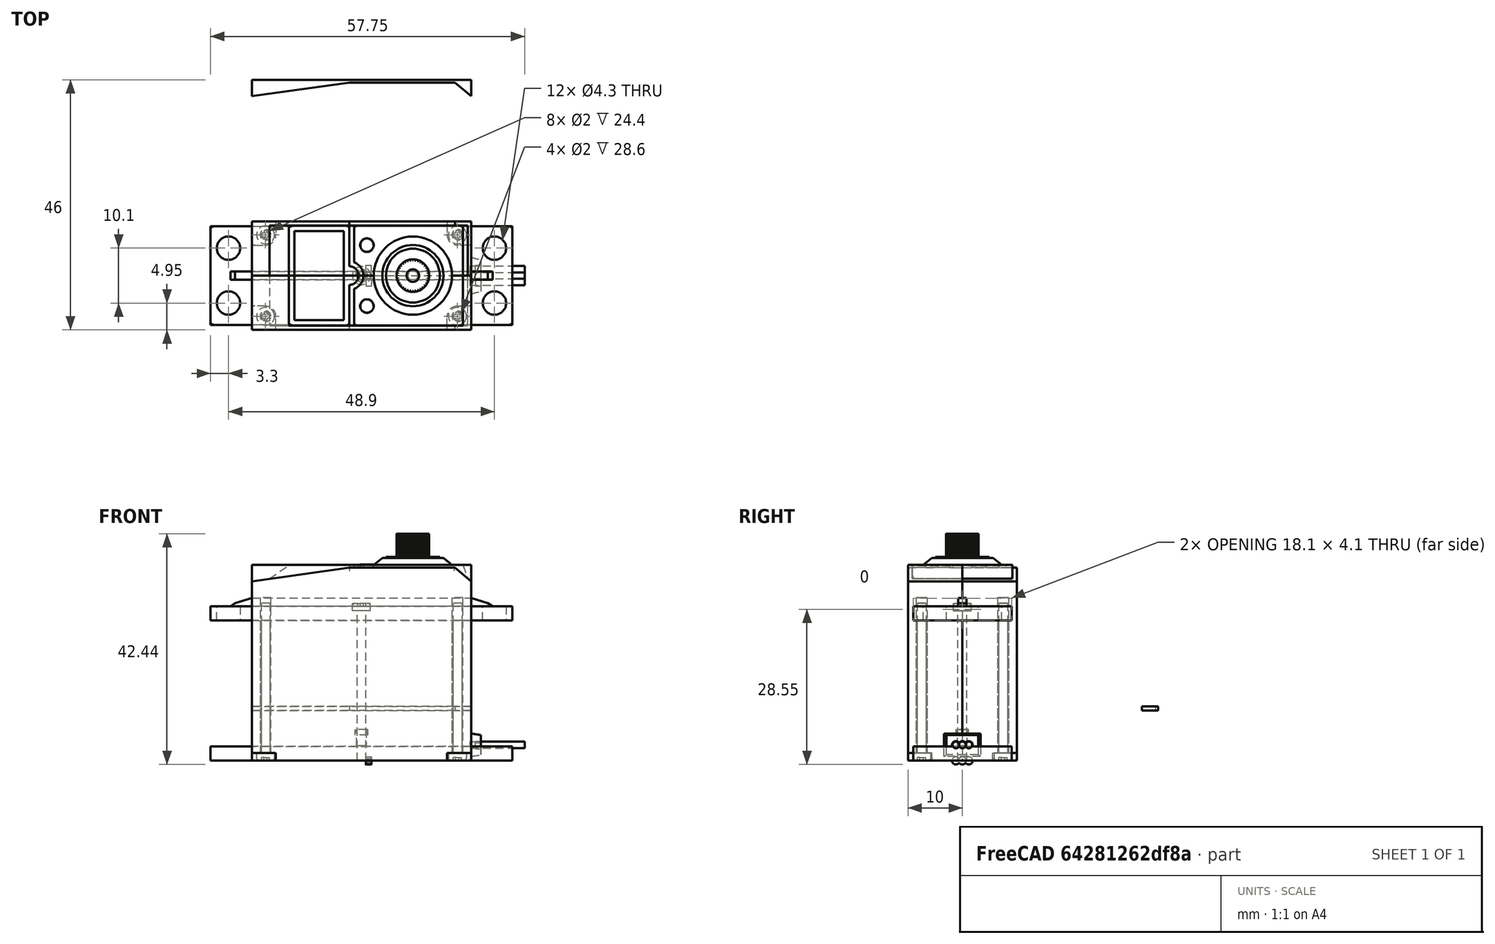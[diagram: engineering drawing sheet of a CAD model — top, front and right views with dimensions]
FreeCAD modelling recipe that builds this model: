
FCSTD DOCUMENT  (FreeCAD 0.15R4671 (Git))
Label: Futaba3003
Comment: It has been modeled using a caliper and a real Futaba 3003 servo
License: CC-BY 3.0
LicenseURL: http://creativecommons.org/licenses/by/3.0/
objects: Sketcher::SketchObject×24, PartDesign::Pocket×12, Part::Feature×12, Part::MultiFuse×7, App::DocumentObjectGroup×6, PartDesign::Pad×5, Part::Loft×3, Part::Cylinder×3, Part::Mirroring×2, Part::Fillet×2, PartDesign::PolarPattern×1, PartDesign::Revolution×1, PartDesign::Fillet×1, PartDesign::Mirrored×1, Part::Cut×1, Part::Compound×1
note: 94 computed .brp shape members not serialized (recipe doc carries the construction recipe); baked Part::Feature solids carry a one-line shape summary decoded from their .brp

FEATURE [Sketcher::SketchObject] Sketch  label="body-sketch"
  Placement = pos=(0,0,0) rot=(1,0,0;1.5708rad)
  sketch-geometry (4):
    g0: LineSegment StartX=-20.15 StartY=36 StartZ=0 EndX=20.15 EndY=36 EndZ=0
    g1: LineSegment StartX=20.15 StartY=0 StartZ=0 EndX=-20.15 EndY=0 EndZ=0
    g2: LineSegment StartX=-20.15 StartY=0 StartZ=0 EndX=-20.15 EndY=36 EndZ=0
    g3: LineSegment StartX=20.15 StartY=36 StartZ=0 EndX=20.15 EndY=0 EndZ=0
  constraints (11):
    c: Coincident(g3,g1)
    c: Coincident(g1,g2)
    c: Horizontal(g0)
    c: Horizontal(g1)
    c: Vertical(g2)
    c: Symmetric(g0,g0,g-2)
    c: PointOnObject(g3,g-1)
    c: DistanceX(g0) = 40.3
    c: DistanceY(g0,g1) = -36
    c: Coincident(g2,g0)
    c: Coincident(g3,g0)
FEATURE [PartDesign::Pad] Pad  label="main_body"
  Length = 10
  Length2 = 100
  Placement = pos=(0,0,0) rot=(1,0,0;1.5708rad)
  Sketch = -> Sketch
  Type = 0
FEATURE [Sketcher::SketchObject] Sketch001  label="lateral-layer1-sketch"
  ExternalGeometry = -> [Pad]
  Placement = pos=(0,-10,0) rot=(1,0,0;1.5708rad)
  Support = -> Pad [Face14]
  sketch-geometry (6):
    g0: LineSegment StartX=20.15 StartY=33 StartZ=0 EndX=17.18 EndY=35.52 EndZ=0
    g1: LineSegment StartX=17.18 StartY=35.52 StartZ=0 EndX=-2.25 EndY=35.52 EndZ=0
    g2: LineSegment StartX=-2.25 StartY=35.52 StartZ=0 EndX=-20.15 EndY=33 EndZ=0
    g3: LineSegment StartX=-20.15 StartY=33 StartZ=0 EndX=-20.15 EndY=36 EndZ=0
    g4: LineSegment StartX=-20.15 StartY=36 StartZ=0 EndX=20.15 EndY=36 EndZ=0
    g5: LineSegment StartX=20.15 StartY=36 StartZ=0 EndX=20.15 EndY=33 EndZ=0
  constraints (16):
    c: Coincident(g0,g1)
    c: Horizontal(g1)
    c: Coincident(g1,g2)
    c: Coincident(g3,g2)
    c: Coincident(g4,g3)
    c: DistanceY(g0) = 33
    c: DistanceY(g4,g0) = -0.48
    c: DistanceX(g0,g0) = -2.97
    c: DistanceX(g4,g1) = -22.4
    c: Coincident(g5,g4)
    c: Coincident(g5,g0)
    c: PointOnObject(g0,g-4)
    c: Coincident(g4,g-4)
    c: Coincident(g3,g-3)
    c: PointOnObject(g2,g-3)
    c: DistanceY(g-1,g2) = 33
FEATURE [Sketcher::SketchObject] Sketch003
  Placement = pos=(0,0,0) rot=(0.57735,0.57735,0.57735;2.0944rad)
  sketch-geometry (4):
    g0: LineSegment StartX=-3.35 StartY=2.1 StartZ=0 EndX=3.35 EndY=2.1 EndZ=0
    g1: LineSegment StartX=3.35 StartY=2.1 StartZ=0 EndX=3.35 EndY=-2.1 EndZ=0
    g2: LineSegment StartX=3.35 StartY=-2.1 StartZ=0 EndX=-3.35 EndY=-2.1 EndZ=0
    g3: LineSegment StartX=-3.35 StartY=-2.1 StartZ=0 EndX=-3.35 EndY=2.1 EndZ=0
  constraints (12):
    c: Coincident(g0,g1)
    c: Coincident(g2,g3)
    c: Coincident(g3,g0)
    c: Horizontal(g0)
    c: Horizontal(g2)
    c: Vertical(g1)
    c: Vertical(g3)
    c: Symmetric(g0,g0,g-2)
    c: Coincident(g1,g2)
    c: DistanceY(g1) = -4.2
    c: DistanceX(g0) = 6.7
    c: Symmetric(g0,g2,g-1)
FEATURE [Sketcher::SketchObject] Sketch004
  Placement = pos=(1.8,0,0) rot=(0.57735,0.57735,0.57735;2.0944rad)
  sketch-geometry (4):
    g0: LineSegment StartX=-2.9 StartY=1.825 StartZ=0 EndX=2.9 EndY=1.825 EndZ=0
    g1: LineSegment StartX=2.9 StartY=1.825 StartZ=0 EndX=2.9 EndY=-1.825 EndZ=0
    g2: LineSegment StartX=2.9 StartY=-1.825 StartZ=0 EndX=-2.9 EndY=-1.825 EndZ=0
    g3: LineSegment StartX=-2.9 StartY=-1.825 StartZ=0 EndX=-2.9 EndY=1.825 EndZ=0
  constraints (12):
    c: Coincident(g0,g1)
    c: Coincident(g2,g3)
    c: Coincident(g3,g0)
    c: Horizontal(g0)
    c: Horizontal(g2)
    c: Vertical(g1)
    c: Vertical(g3)
    c: Symmetric(g0,g0,g-2)
    c: Coincident(g1,g2)
    c: DistanceY(g1) = -3.65
    c: DistanceX(g0) = 5.8
    c: Symmetric(g0,g2,g-1)
FEATURE [Part::Loft] Loft  label="wire-holder-body"
  Closed = false
  Placement = pos=(20.15,0,2.9) rot=(0,0,1;0rad)
  Ruled = false
  Sections = -> [Sketch003,Sketch004]
  Solid = true
FEATURE [Part::Cylinder] Cylinder  label="red-wire"
  Angle = 360
  Height = 10
  Placement = pos=(0,0,0) rot=(0,1,0;1.5708rad)
  Radius = 0.6
FEATURE [Part::Cylinder] Cylinder001  label="white-wire"
  Angle = 360
  Height = 10
  Placement = pos=(0,1.2,0) rot=(0,1,0;1.5708rad)
  Radius = 0.6
FEATURE [Part::Cylinder] Cylinder002  label="blck-wire"
  Angle = 360
  Height = 10
  Placement = pos=(0,-1.2,0) rot=(0,1,0;1.5708rad)
  Radius = 0.6
FEATURE [Sketcher::SketchObject] Sketch005
  ExternalGeometry = -> [Loft]
  Placement = pos=(21.95,0,2.9) rot=(0.57735,0.57735,0.57735;2.0944rad)
  Support = -> Loft [Face6]
  sketch-geometry (6):
    g0: LineSegment [constr] StartX=-1.2 StartY=0 StartZ=0 EndX=1.2 EndY=0 EndZ=0
    g1: ArcOfCircle CenterX=-1.2 CenterY=0 CenterZ=0 NormalX=0 NormalY=0 NormalZ=1 Radius=0.7 StartAngle=0.5411 EndAngle=5.74209
    g2: ArcOfCircle CenterX=0 CenterY=0 CenterZ=0 NormalX=0 NormalY=0 NormalZ=1 Radius=0.7 StartAngle=0.5411 EndAngle=2.60049
    g3: ArcOfCircle CenterX=0 CenterY=0 CenterZ=0 NormalX=0 NormalY=0 NormalZ=1 Radius=0.7 StartAngle=3.68269 EndAngle=5.74209
    g4: ArcOfCircle CenterX=1.2 CenterY=0 CenterZ=0 NormalX=0 NormalY=0 NormalZ=1 Radius=0.7 StartAngle=3.68269 EndAngle=8.88368
    g5: LineSegment [constr] StartX=-1.2 StartY=0 StartZ=0 EndX=-1.2 EndY=-0.7 EndZ=0
  constraints (20):
    c: Horizontal(g0)
    c: Symmetric(g0,g0,g-2)
    c: Coincident(g1,g0)
    c: PointOnObject(g2,g0)
    c: Coincident(g2,g1)
    c: PointOnObject(g2,g-2)
    c: Coincident(g3,g2)
    c: Coincident(g3,g1)
    c: Coincident(g4,g0)
    c: Coincident(g4,g2)
    c: Coincident(g4,g3)
    c: Equal(g1,g2)
    c: Equal(g2,g4)
    c: Equal(g4,g3)
    c: DistanceX(g2,g0) = 1.2
    c: Coincident(g5,g0)
    c: Vertical(g5)
    c: PointOnObject(g5,g1)
    c: Radius(g4) = 0.7
    c: PointOnObject(g0,g-1)
FEATURE [PartDesign::Pocket] Pocket002  label="wire-holder"
  Length = 1
  Placement = pos=(20.15,0,2.9) rot=(0,0,1;0rad)
  Sketch = -> Sketch005
  Type = 0
FEATURE [App::DocumentObjectGroup] Group  label="servo-wire-holder"
  Group = -> [Pocket002,Loft]
FEATURE [PartDesign::Pocket] Pocket  label="lateral-layer1"
  Length = 0.8
  Placement = pos=(0,0,0) rot=(1,0,0;1.5708rad)
  Sketch = -> Sketch001
  Type = 0
FEATURE [Sketcher::SketchObject] Sketch002  label="lateral-layer2-sketch"
  Placement = pos=(0,-9.2,0) rot=(1,0,0;1.5708rad)
  Support = -> Pocket [Face4]
  sketch-geometry (12):
    g0: GeomPoint [constr] X=19.55 Y=33.5091 Z=0
    g1: GeomPoint [constr] X=18.65 Y=36 Z=0
    g2: LineSegment StartX=18.65 StartY=36 StartZ=0 EndX=19.55 EndY=33.5091 EndZ=0
    g3: LineSegment StartX=19.55 StartY=33.5091 StartZ=0 EndX=20.15 EndY=33 EndZ=0
    g4: LineSegment StartX=18.65 StartY=36 StartZ=0 EndX=20.15 EndY=36 EndZ=0
    g5: LineSegment StartX=20.15 StartY=36 StartZ=0 EndX=20.15 EndY=33 EndZ=0
    g6: GeomPoint [constr] X=-16.9 Y=33.4575 Z=0
    g7: GeomPoint [constr] X=-13.35 Y=36 Z=0
    g8: LineSegment StartX=-20.15 StartY=33 StartZ=0 EndX=-16.9 EndY=33.4575 EndZ=0
    g9: LineSegment StartX=-16.9 StartY=33.4575 StartZ=0 EndX=-13.35 EndY=36 EndZ=0
    g10: LineSegment StartX=-20.15 StartY=33 StartZ=0 EndX=-20.15 EndY=36 EndZ=0
    g11: LineSegment StartX=-20.15 StartY=36 StartZ=0 EndX=-13.35 EndY=36 EndZ=0
  constraints (16):
    c: Coincident(g2,g1)
    c: Coincident(g2,g0)
    c: Coincident(g4,g1)
    c: Coincident(g5,g4)
    c: Coincident(g5,g3)
    c: Coincident(g3,g0)
    c: Coincident(g8,g6)
    c: Coincident(g9,g6)
    c: Coincident(g9,g7)
    c: DistanceX(g8,g6) = 3.25
    c: DistanceX(g7,g4) = 33.5
    c: Coincident(g10,g8)
    c: Coincident(g11,g10)
    c: Coincident(g11,g7)
    c: DistanceX(g4,g0) = -0.6
    c: DistanceX(g1,g4) = 1.5
FEATURE [PartDesign::Pocket] Pocket003  label="lateral-layer2"
  Length = 5
  Placement = pos=(0,0,0) rot=(1,0,0;1.5708rad)
  Sketch = -> Sketch002
  Type = 1
FEATURE [Part::Mirroring] Part__Mirroring  label="lateral-layer2 (Mirror #1)"
  Base = (0,0,0)
  Normal = (0,1,0)
  Source = -> Pocket003
FEATURE [Sketcher::SketchObject] Sketch006  label="ear-body-sketch"
  sketch-geometry (4):
    g0: LineSegment StartX=-27.75 StartY=9.05 StartZ=0 EndX=27.75 EndY=9.05 EndZ=0
    g1: LineSegment StartX=27.75 StartY=9.05 StartZ=0 EndX=27.75 EndY=-9.05 EndZ=0
    g2: LineSegment StartX=27.75 StartY=-9.05 StartZ=0 EndX=-27.75 EndY=-9.05 EndZ=0
    g3: LineSegment StartX=-27.75 StartY=-9.05 StartZ=0 EndX=-27.75 EndY=9.05 EndZ=0
  constraints (11):
    c: Coincident(g0,g1)
    c: Coincident(g1,g2)
    c: Coincident(g2,g3)
    c: Coincident(g3,g0)
    c: Horizontal(g0)
    c: Horizontal(g2)
    c: Vertical(g1)
    c: Vertical(g3)
    c: Symmetric(g0,g1,g-1)
    c: DistanceX(g0) = 55.5
    c: DistanceY(g1) = -18.1
FEATURE [PartDesign::Pad] Pad001  label="ear-body"
  Length = 2.6
  Length2 = 100
  Sketch = -> Sketch006
  Type = 0
FEATURE [Sketcher::SketchObject] Sketch007  label="ear-holes-sketch"
  Placement = pos=(0,0,2.6) rot=(0,0,1;0rad)
  Support = -> Pad001 [Face6]
  sketch-geometry (12):
    g0: Circle CenterX=-24.45 CenterY=5.05 CenterZ=0 NormalX=0 NormalY=0 NormalZ=1 Radius=2.15
    g1: Circle CenterX=-24.45 CenterY=-5.05 CenterZ=0 NormalX=0 NormalY=0 NormalZ=1 Radius=2.15
    g2: Circle CenterX=24.45 CenterY=5.05 CenterZ=0 NormalX=0 NormalY=0 NormalZ=1 Radius=2.15
    g3: Circle CenterX=24.45 CenterY=-5.05 CenterZ=0 NormalX=0 NormalY=0 NormalZ=1 Radius=2.15
    g4: LineSegment [constr] StartX=-24.45 StartY=5.05 StartZ=0 EndX=24.45 EndY=5.05 EndZ=0
    g5: LineSegment [constr] StartX=24.45 StartY=5.05 StartZ=0 EndX=24.45 EndY=-5.05 EndZ=0
    g6: LineSegment [constr] StartX=24.45 StartY=-5.05 StartZ=0 EndX=-24.45 EndY=-5.05 EndZ=0
    g7: LineSegment [constr] StartX=-24.45 StartY=-5.05 StartZ=0 EndX=-24.45 EndY=5.05 EndZ=0
    g8: GeomPoint [constr] X=-24.45 Y=2.9 Z=0
    g9: GeomPoint [constr] X=-22.3 Y=5.05 Z=0
    g10: GeomPoint [constr] X=-24.45 Y=-2.9 Z=0
    g11: GeomPoint [constr] X=22.3 Y=5.05 Z=0
  constraints (27):
    c: Coincident(g4,g5)
    c: Coincident(g5,g6)
    c: Coincident(g6,g7)
    c: Coincident(g7,g4)
    c: Horizontal(g4)
    c: Horizontal(g6)
    c: Vertical(g5)
    c: Vertical(g7)
    c: Symmetric(g4,g5,g-1)
    c: Coincident(g2,g4)
    c: Coincident(g3,g5)
    c: Coincident(g1,g6)
    c: Coincident(g0,g4)
    c: PointOnObject(g8,g7)
    c: PointOnObject(g9,g4)
    c: PointOnObject(g8,g0)
    c: PointOnObject(g9,g0)
    c: Equal(g0,g1)
    c: Equal(g1,g2)
    c: Equal(g2,g3)
    c: Radius(g0) = 2.15
    c: PointOnObject(g10,g7)
    c: PointOnObject(g10,g1)
    c: DistanceY(g8,g10) = -5.8
    c: PointOnObject(g11,g4)
    c: PointOnObject(g11,g2)
    c: DistanceX(g9,g11) = 44.6
FEATURE [PartDesign::Pocket] Pocket004  label="ear-holes"
  Length = 5
  Sketch = -> Sketch007
  Type = 1
FEATURE [Sketcher::SketchObject] Sketch008  label="nose-sketch"
  Placement = pos=(0,0,2.6) rot=(1,0,0;1.5708rad)
  sketch-geometry (6):
    g0: LineSegment StartX=-24.1 StartY=0 StartZ=0 EndX=-23.23 EndY=0.6 EndZ=0
    g1: LineSegment StartX=-23.23 StartY=0.6 StartZ=0 EndX=-20.15 EndY=1.5 EndZ=0
    g2: LineSegment StartX=-20.15 StartY=1.5 StartZ=0 EndX=20.15 EndY=1.5 EndZ=0
    g3: LineSegment StartX=20.15 StartY=1.5 StartZ=0 EndX=23.23 EndY=0.6 EndZ=0
    g4: LineSegment StartX=23.23 StartY=0.6 StartZ=0 EndX=24.1 EndY=0 EndZ=0
    g5: LineSegment StartX=24.1 StartY=0 StartZ=0 EndX=-24.1 EndY=0 EndZ=0
  constraints (17):
    c: PointOnObject(g0,g-1)
    c: Coincident(g0,g1)
    c: Coincident(g1,g2)
    c: Horizontal(g2)
    c: Coincident(g2,g3)
    c: Coincident(g3,g4)
    c: PointOnObject(g4,g-1)
    c: Coincident(g4,g5)
    c: Coincident(g5,g0)
    c: DistanceX(g2) = 40.3
    c: Symmetric(g1,g2,g-2)
    c: Symmetric(g3,g0,g-2)
    c: Symmetric(g0,g4,g-2)
    c: DistanceX(g0,g4) = 48.2
    c: DistanceX(g0,g1) = 3.08
    c: DistanceY(g0,g1) = 1.5
    c: DistanceY(g0,g0) = -0.6
FEATURE [PartDesign::Pad] Pad002  label="nose"
  Length = 1.5
  Length2 = 100
  Midplane = true
  Placement = pos=(0,0,2.6) rot=(1,0,0;1.5708rad)
  Sketch = -> Sketch008
  Type = 0
FEATURE [Sketcher::SketchObject] Sketch010
  sketch-geometry (1):
    g0: Circle CenterX=0 CenterY=0 CenterZ=0 NormalX=0 NormalY=0 NormalZ=1 Radius=7.2
  constraints (2):
    c: Coincident(g0,g-1)
    c: Radius(g0) = 7.2
FEATURE [Sketcher::SketchObject] Sketch011
  Placement = pos=(0,0,1.3) rot=(0,0,1;0rad)
  sketch-geometry (1):
    g0: Circle CenterX=0 CenterY=0 CenterZ=0 NormalX=0 NormalY=0 NormalZ=1 Radius=5.625
  constraints (2):
    c: Coincident(g0,g-1)
    c: Radius(g0) = 5.625
FEATURE [Part::Loft] Loft001  label="shaft-base1"
  Closed = false
  Placement = pos=(9.45,0,36) rot=(0,0,1;0rad)
  Ruled = false
  Sections = -> [Sketch010,Sketch011]
  Solid = true
FEATURE [Sketcher::SketchObject] Sketch012
  Placement = pos=(9.45,0,37.3) rot=(0,0,1;0rad)
  Support = -> Loft001 [Face3]
  sketch-geometry (1):
    g0: Circle CenterX=0 CenterY=0 CenterZ=0 NormalX=0 NormalY=0 NormalZ=1 Radius=4.95
  constraints (2):
    c: Coincident(g0,g-1)
    c: Radius(g0) = 4.95
FEATURE [PartDesign::Pad] Pad005  label="shaft-base2"
  Length = 0.2
  Length2 = 100
  Placement = pos=(9.45,0,36) rot=(0,0,1;0rad)
  Sketch = -> Sketch012
  Type = 0
FEATURE [Sketcher::SketchObject] Sketch013
  Placement = pos=(9.45,0,37.5) rot=(0,0,1;0rad)
  Support = -> Pad005 [Face5]
  sketch-geometry (1):
    g0: Circle CenterX=0 CenterY=0 CenterZ=0 NormalX=0 NormalY=0 NormalZ=1 Radius=3
  constraints (2):
    c: Coincident(g0,g-1)
    c: Radius(g0) = 3
FEATURE [PartDesign::Pad] Pad006  label="base-plus-basic-shaft"
  Length = 4.24
  Length2 = 100
  Placement = pos=(9.45,0,36) rot=(0,0,1;0rad)
  Sketch = -> Sketch013
  Type = 0
FEATURE [Sketcher::SketchObject] Sketch014  label="master-tooth-sketch"
  ExternalGeometry = -> [Pad006]
  Placement = pos=(9.45,0,41.74) rot=(0,0,1;0rad)
  Support = -> Pad006 [Face7]
  sketch-geometry (8):
    g0: Circle [constr] CenterX=0 CenterY=0 CenterZ=0 NormalX=0 NormalY=0 NormalZ=1 Radius=3.2
    g1: Circle [constr] CenterX=0 CenterY=0 CenterZ=0 NormalX=0 NormalY=0 NormalZ=1 Radius=2.8
    g2: LineSegment StartX=-0.1 StartY=3.19844 StartZ=0 EndX=0.1 EndY=3.19844 EndZ=0
    g3: LineSegment [constr] StartX=-0.1 StartY=3.19844 StartZ=0 EndX=0 EndY=0 EndZ=0
    g4: LineSegment [constr] StartX=0.1 StartY=3.19844 StartZ=0 EndX=0 EndY=0 EndZ=0
    g5: LineSegment StartX=-0.1 StartY=3.19844 StartZ=0 EndX=-0.0875 EndY=2.79863 EndZ=0
    g6: LineSegment StartX=-0.0875 StartY=2.79863 StartZ=0 EndX=0.0875 EndY=2.79863 EndZ=0
    g7: LineSegment StartX=0.0875 StartY=2.79863 StartZ=0 EndX=0.1 EndY=3.19844 EndZ=0
  constraints (20):
    c: Coincident(g0,g-1)
    c: Radius(g0) = 3.2
    c: Coincident(g1,g-1)
    c: Radius(g1) = 2.8
    c: Horizontal(g2)
    c: PointOnObject(g2,g0)
    c: PointOnObject(g2,g0)
    c: DistanceX(g2,g2) = 0.2
    c: Coincident(g3,g2)
    c: Coincident(g2,g4)
    c: Coincident(g4,g-1)
    c: Coincident(g3,g-1)
    c: Coincident(g5,g6)
    c: Coincident(g6,g7)
    c: Coincident(g5,g2)
    c: Coincident(g7,g2)
    c: PointOnObject(g5,g3)
    c: PointOnObject(g6,g4)
    c: PointOnObject(g5,g1)
    c: PointOnObject(g6,g1)
FEATURE [PartDesign::Pocket] Pocket005  label="master-tooth"
  Length = 4.1
  Placement = pos=(9.45,0,36) rot=(0,0,1;0rad)
  Sketch = -> Sketch014
  Type = 0
FEATURE [PartDesign::PolarPattern] PolarPattern  label="shaft-teeth"
  Angle = 360
  Axis = -> Sketch014 [N_Axis]
  Occurrences = 36
  Originals = -> [Pocket005]
  Placement = pos=(9.45,0,36) rot=(0,0,1;0rad)
FEATURE [Sketcher::SketchObject] Sketch017  label="top-cone-top"
  sketch-geometry (1):
    g0: Circle CenterX=0 CenterY=0 CenterZ=0 NormalX=0 NormalY=0 NormalZ=1 Radius=1.1
  constraints (2):
    c: Coincident(g0,g-1)
    c: Radius(g0) = 1.1
FEATURE [Sketcher::SketchObject] Sketch018  label="top-cone-bottom"
  Placement = pos=(0,0,0.6) rot=(0,0,1;0rad)
  sketch-geometry (1):
    g0: Circle CenterX=0 CenterY=0 CenterZ=0 NormalX=0 NormalY=0 NormalZ=1 Radius=1.25
  constraints (2):
    c: Coincident(g0,g-1)
    c: Radius(g0) = 1.25
FEATURE [Sketcher::SketchObject] Sketch021
  Placement = pos=(0,0,0) rot=(1,0,0;1.5708rad)
  sketch-geometry (6):
    g0: LineSegment StartX=0 StartY=0 StartZ=0 EndX=0.81 EndY=0 EndZ=0
    g1: LineSegment StartX=0.81 StartY=0 StartZ=0 EndX=0.81 EndY=27.6 EndZ=0
    g2: LineSegment StartX=0 StartY=28.9 StartZ=0 EndX=0 EndY=0 EndZ=0
    g3: LineSegment StartX=0.81 StartY=27.6 StartZ=0 EndX=1.65 EndY=27.6 EndZ=0
    g4: LineSegment StartX=1.65 StartY=27.6 StartZ=0 EndX=1.65 EndY=28.9 EndZ=0
    g5: LineSegment StartX=1.65 StartY=28.9 StartZ=0 EndX=0 EndY=28.9 EndZ=0
  constraints (17):
    c: Coincident(g0,g1)
    c: Coincident(g2,g0)
    c: Horizontal(g0)
    c: Vertical(g1)
    c: Vertical(g2)
    c: Coincident(g0,g-1)
    c: Coincident(g3,g4)
    c: Coincident(g4,g5)
    c: Coincident(g2,g5)
    c: Horizontal(g5)
    c: Coincident(g3,g1)
    c: Horizontal(g3)
    c: Vertical(g4)
    c: DistanceY(g2) = -28.9
    c: DistanceX(g0) = 0.81
    c: DistanceX(g5) = -1.65
    c: DistanceY(g4) = 1.3
FEATURE [PartDesign::Revolution] Revolution  label="screw-shape"
  Angle = 360
  Axis = (0,0,1)
  Base = (0,0,0)
  Placement = pos=(0,0,0) rot=(1,0,0;1.5708rad)
  ReferenceAxis = -> Sketch021 [V_Axis]
  Reversed = true
  Sketch = -> Sketch021
FEATURE [Sketcher::SketchObject] Sketch022  label="screw-cross-sketch"
  Placement = pos=(0,0,28.9) rot=(0,0,1;3.14159rad)
  Support = -> Revolution [Face5]
  sketch-geometry (12):
    g0: LineSegment StartX=-0.3 StartY=0.75 StartZ=0 EndX=0.3 EndY=0.75 EndZ=0
    g1: LineSegment StartX=0.3 StartY=0.75 StartZ=0 EndX=0.3 EndY=0.3 EndZ=0
    g2: LineSegment StartX=0.3 StartY=-0.75 StartZ=0 EndX=-0.3 EndY=-0.75 EndZ=0
    g3: LineSegment StartX=-0.3 StartY=-0.75 StartZ=0 EndX=-0.3 EndY=-0.3 EndZ=0
    g4: LineSegment StartX=-0.75 StartY=0.3 StartZ=0 EndX=-0.3 EndY=0.3 EndZ=0
    g5: LineSegment StartX=0.75 StartY=0.3 StartZ=0 EndX=0.75 EndY=-0.3 EndZ=0
    g6: LineSegment StartX=0.75 StartY=-0.3 StartZ=0 EndX=0.3 EndY=-0.3 EndZ=0
    g7: LineSegment StartX=-0.75 StartY=-0.3 StartZ=0 EndX=-0.75 EndY=0.3 EndZ=0
    g8: LineSegment StartX=-0.3 StartY=0.3 StartZ=0 EndX=-0.3 EndY=0.75 EndZ=0
    g9: LineSegment StartX=0.3 StartY=-0.3 StartZ=0 EndX=0.3 EndY=-0.75 EndZ=0
    g10: LineSegment StartX=0.3 StartY=0.3 StartZ=0 EndX=0.75 EndY=0.3 EndZ=0
    g11: LineSegment StartX=-0.3 StartY=-0.3 StartZ=0 EndX=-0.75 EndY=-0.3 EndZ=0
  constraints (30):
    c: Coincident(g0,g1)
    c: Coincident(g9,g2)
    c: Coincident(g2,g3)
    c: Coincident(g8,g0)
    c: Horizontal(g0)
    c: Horizontal(g2)
    c: Vertical(g1)
    c: Vertical(g3)
    c: Symmetric(g0,g9,g-1)
    c: Coincident(g10,g5)
    c: Coincident(g5,g6)
    c: Coincident(g11,g7)
    c: Coincident(g7,g4)
    c: Horizontal(g4)
    c: Horizontal(g6)
    c: Vertical(g5)
    c: Vertical(g7)
    c: Symmetric(g4,g5,g-1)
    c: Tangent(g3,g8)
    c: Tangent(g1,g9)
    c: Coincident(g4,g8)
    c: Coincident(g10,g1)
    c: Tangent(g4,g10)
    c: Coincident(g6,g9)
    c: Coincident(g11,g3)
    c: Tangent(g6,g11)
    c: Equal(g0,g7)
    c: Equal(g8,g4)
    c: DistanceX(g4,g5) = 1.5
    c: DistanceX(g0) = 0.6
FEATURE [PartDesign::Pocket] Pocket002006
  Length = 0.5
  Placement = pos=(0,0,0) rot=(1,0,0;1.5708rad)
  Sketch = -> Sketch022
  Type = 0
FEATURE [PartDesign::Fillet] Fillet  label="servo-screw-final1"
  Base = -> Pocket002006 [Edge5]
  Placement = pos=(0,0,0) rot=(1,0,0;1.5708rad)
  Radius = 0.4
FEATURE [Part::Feature] Fillet001  label="servo-screw1"
  Placement = pos=(17.6429,-7.49289,29) rot=(-1,0,0;1.5708rad)
  shape: bbox 3.572 x 3.572 x 28.9 mm, 19 faces (baked)
FEATURE [Part::Feature] Fillet001001  label="servo-screw002"
  Placement = pos=(-17.6429,-7.49289,29) rot=(-1,0,0;1.5708rad)
  shape: bbox 3.572 x 3.572 x 28.9 mm, 19 faces (baked)
FEATURE [Part::Feature] Fillet001002  label="servo-screw003"
  Placement = pos=(-17.6429,7.49289,29) rot=(-1,0,0;1.5708rad)
  shape: bbox 3.572 x 3.572 x 28.9 mm, 19 faces (baked)
FEATURE [Part::Feature] Fillet001003  label="servo-screw004"
  Placement = pos=(17.6429,7.49289,29) rot=(-1,0,0;1.5708rad)
  shape: bbox 3.572 x 3.572 x 28.9 mm, 19 faces (baked)
FEATURE [Sketcher::SketchObject] Sketch023
  Placement = pos=(9.45,0,41.74) rot=(0,0,1;0rad)
  Support = -> PolarPattern [Face9]
  sketch-geometry (1):
    g0: Circle CenterX=0 CenterY=0 CenterZ=0 NormalX=0 NormalY=0 NormalZ=1 Radius=0.9
  constraints (2):
    c: Coincident(g0,g-1)
    c: Radius(g0) = 0.9
FEATURE [PartDesign::Pocket] Pocket002007  label="shaft-drill-1"
  Length = 3
  Placement = pos=(9.45,0,36) rot=(0,0,1;0rad)
  Sketch = -> Sketch023
  Type = 0
FEATURE [Sketcher::SketchObject] Sketch024
  Placement = pos=(9.45,0,41.74) rot=(0,0,1;0rad)
  Support = -> Pocket002007 [Face9]
  sketch-geometry (1):
    g0: Circle CenterX=0 CenterY=0 CenterZ=0 NormalX=0 NormalY=0 NormalZ=1 Radius=1.15
  constraints (2):
    c: Coincident(g0,g-1)
    c: Radius(g0) = 1.15
FEATURE [PartDesign::Pocket] Pocket002008  label="shaft-drill-2"
  Length = 1
  Placement = pos=(9.45,0,36) rot=(0,0,1;0rad)
  Sketch = -> Sketch024
  Type = 0
FEATURE [App::DocumentObjectGroup] Group002  label="servo-shaft"
  Group = -> [Loft001,Pad005,Pad006,Pocket005,PolarPattern,Pocket002007,Pocket002008]
FEATURE [Part::Loft] Loft002  label="top-cone-master"
  Closed = false
  Placement = pos=(1,5.6,35.5) rot=(0,0,1;0rad)
  Ruled = false
  Sections = -> [Sketch017,Sketch018]
  Solid = true
FEATURE [Part::MultiFuse] Fusion006  label="servo-body001"
  Shapes = -> [Pocket003,Part__Mirroring]
FEATURE [Sketcher::SketchObject] Sketch015  label="top-details-1-sketch"
  ExternalGeometry = -> [Fusion006]
  Placement = pos=(0,0,36) rot=(0,0,1;0rad)
  Support = -> Fusion006 [Face8]
  sketch-geometry (10):
    g0: ArcOfCircle CenterX=-2.25 CenterY=0 CenterZ=0 NormalX=0 NormalY=0 NormalZ=1 Radius=1.7 StartAngle=4.71239 EndAngle=7.85398
    g1: LineSegment StartX=-2.25 StartY=9.2 StartZ=0 EndX=-2.25 EndY=1.7 EndZ=0
    g2: LineSegment StartX=-2.25 StartY=-1.7 StartZ=0 EndX=-2.25 EndY=-9.2 EndZ=0
    g3: ArcOfCircle CenterX=-2.25 CenterY=0 CenterZ=0 NormalX=0 NormalY=0 NormalZ=1 Radius=2.6 StartAngle=5.06586 EndAngle=7.50051
    g4: LineSegment [constr] StartX=-0.55 StartY=0 StartZ=0 EndX=0.35 EndY=0 EndZ=0
    g5: LineSegment [constr] StartX=-1.35 StartY=2.43926 StartZ=0 EndX=-2.25 EndY=2.43926 EndZ=0
    g6: LineSegment StartX=-1.35 StartY=2.43926 StartZ=0 EndX=-1.35 EndY=9.2 EndZ=0
    g7: LineSegment StartX=-2.25 StartY=9.2 StartZ=0 EndX=-1.35 EndY=9.2 EndZ=0
    g8: LineSegment StartX=-1.35 StartY=-2.43926 StartZ=0 EndX=-1.35 EndY=-9.2 EndZ=0
    g9: LineSegment StartX=-2.25 StartY=-9.2 StartZ=0 EndX=-1.35 EndY=-9.2 EndZ=0
  constraints (30):
    c: Radius(g0) = 1.7
    c: Symmetric(g0,g0,g-1)
    c: Coincident(g1,g0)
    c: Vertical(g1)
    c: Vertical(g2)
    c: Coincident(g2,g0)
    c: PointOnObject(g0,g1)
    c: Symmetric(g3,g3,g-1)
    c: PointOnObject(g4,g-1)
    c: Horizontal(g4)
    c: PointOnObject(g4,g0)
    c: PointOnObject(g4,g3)
    c: Coincident(g3,g0)
    c: DistanceX(g4) = 0.9
    c: Horizontal(g5)
    c: PointOnObject(g5,g1)
    c: Vertical(g6)
    c: Horizontal(g7)
    c: Coincident(g7,g1)
    c: Coincident(g7,g6)
    c: Coincident(g6,g3)
    c: DistanceX(g5) = -0.9
    c: Coincident(g5,g3)
    c: Coincident(g8,g3)
    c: Vertical(g8)
    c: Coincident(g9,g2)
    c: Horizontal(g9)
    c: Coincident(g9,g8)
    c: Symmetric(g1,g2,g-1)
    c: Coincident(g1,g-3)
FEATURE [PartDesign::Pocket] Pocket002008004  label="top-details-1"
  Length = 0.48
  Sketch = -> Sketch015
  Type = 0
FEATURE [Sketcher::SketchObject] Sketch016  label="top-details-2-sketch"
  ExternalGeometry = -> [Pocket002008004]
  Placement = pos=(0,0,36) rot=(0,0,1;0rad)
  Support = -> Pocket002008004 [Face21]
  sketch-geometry (6):
    g0: LineSegment StartX=-12.35 StartY=8.2 StartZ=0 EndX=-3.25 EndY=8.2 EndZ=0
    g1: LineSegment StartX=-3.25 StartY=8.2 StartZ=0 EndX=-3.25 EndY=-8.2 EndZ=0
    g2: LineSegment StartX=-3.25 StartY=-8.2 StartZ=0 EndX=-12.35 EndY=-8.2 EndZ=0
    g3: LineSegment StartX=-12.35 StartY=-8.2 StartZ=0 EndX=-12.35 EndY=8.2 EndZ=0
    g4: LineSegment [constr] StartX=-13.35 StartY=9.2 StartZ=0 EndX=-12.35 EndY=8.2 EndZ=0
    g5: LineSegment [constr] StartX=-2.25 StartY=-9.2 StartZ=0 EndX=-3.25 EndY=-8.2 EndZ=0
  constraints (16):
    c: Coincident(g4,g0)
    c: Coincident(g0,g3)
    c: Horizontal(g0)
    c: Vertical(g3)
    c: Coincident(g0,g1)
    c: Vertical(g1)
    c: Coincident(g2,g3)
    c: Horizontal(g2)
    c: Coincident(g1,g2)
    c: Coincident(g5,g1)
    c: DistanceX(g0,g4) = -1
    c: DistanceX(g5,g1) = -1
    c: Coincident(g4,g-3)
    c: Angle(g-3,g4) = 0.785398
    c: Coincident(g5,g-4)
    c: Angle(g5,g-1) = 0.785398
FEATURE [PartDesign::Pocket] Pocket002008007002  label="top-details-2"
  Length = 0.1
  Sketch = -> Sketch016
  Type = 0
FEATURE [Sketcher::SketchObject] Sketch025  label="bottom-details-1-sketch"
  ExternalGeometry = -> [Pocket002008007002]
  Placement = pos=(0,0,0) rot=(1,0,0;3.14159rad)
  Support = -> Pocket002008007002 [Face17]
  sketch-geometry (12):
    g0: LineSegment StartX=-17.6429 StartY=5.6 StartZ=0 EndX=-20.15 EndY=5.6 EndZ=0
    g1: LineSegment StartX=-20.15 StartY=5.6 StartZ=0 EndX=-20.15 EndY=10 EndZ=0
    g2: LineSegment StartX=-15.75 StartY=10 StartZ=0 EndX=-15.75 EndY=7.49289 EndZ=0
    g3: ArcOfCircle CenterX=-17.6429 CenterY=7.49289 CenterZ=0 NormalX=0 NormalY=0 NormalZ=1 Radius=1.89289 StartAngle=4.7124 EndAngle=6.28319
    g4: Circle [constr] CenterX=-17.6429 CenterY=7.49289 CenterZ=0 NormalX=0 NormalY=0 NormalZ=1 Radius=1
    g5: LineSegment StartX=-20.15 StartY=10 StartZ=0 EndX=-15.75 EndY=10 EndZ=0
    g6: LineSegment [constr] StartX=-20.15 StartY=10 StartZ=0 EndX=-18.35 EndY=8.2 EndZ=0
    g7: LineSegment StartX=-20.15 StartY=-5.6 StartZ=0 EndX=-20.15 EndY=-10 EndZ=0
    g8: LineSegment StartX=-20.15 StartY=-5.6 StartZ=0 EndX=-17.6429 EndY=-5.6 EndZ=0
    g9: LineSegment StartX=-20.15 StartY=-10 StartZ=0 EndX=-15.75 EndY=-10 EndZ=0
    g10: LineSegment StartX=-15.75 StartY=-10 StartZ=0 EndX=-15.75 EndY=-7.49289 EndZ=0
    g11: ArcOfCircle CenterX=-17.6429 CenterY=-7.49289 CenterZ=0 NormalX=0 NormalY=0 NormalZ=1 Radius=1.89289 StartAngle=6.28318 EndAngle=7.85397
  constraints (34):
    c: Coincident(g0,g1)
    c: Vertical(g2)
    c: Horizontal(g0)
    c: Vertical(g1)
    c: Coincident(g3,g2)
    c: Coincident(g3,g0)
    c: Tangent(g3,g0)
    c: Radius(g4) = 1
    c: Coincident(g3,g4)
    c: Coincident(g5,g1)
    c: Coincident(g5,g2)
    c: Horizontal(g5)
    c: Coincident(g6,g1)
    c: Angle(g6,g5) = 0.785398
    c: PointOnObject(g6,g4)
    c: PointOnObject(g3,g6)
    c: DistanceX(g5) = 4.4
    c: DistanceX(g6,g1) = -1.8
    c: Coincident(g1,g-3)
    c: Tangent(g2,g3)
    c: Vertical(g7)
    c: Symmetric(g7,g1,g-1)
    c: Symmetric(g7,g0,g-1)
    c: Horizontal(g8)
    c: Coincident(g8,g7)
    c: Symmetric(g8,g0,g-1)
    c: Horizontal(g9)
    c: Coincident(g9,g7)
    c: Symmetric(g9,g2,g-1)
    c: Coincident(g10,g9)
    c: Symmetric(g10,g2,g-1)
    c: Coincident(g11,g8)
    c: Coincident(g11,g10)
    c: Symmetric(g11,g3,g-1)
FEATURE [PartDesign::Pocket] Pocket002008007003  label="bottom-details-1"
  Length = 1.4
  Sketch = -> Sketch025
  Type = 0
FEATURE [PartDesign::Mirrored] Mirrored  label="bottom-details-1-complete"
  MirrorPlane = -> Sketch025 [V_Axis]
  Originals = -> [Pocket002008007003]
FEATURE [Sketcher::SketchObject] Sketch026  label="bottom-drills-sketch"
  ExternalGeometry = -> [Mirrored]
  Placement = pos=(0,0,0) rot=(1,0,0;3.14159rad)
  Support = -> Mirrored [Face19]
  sketch-geometry (6):
    g0: Circle CenterX=-17.6429 CenterY=7.49289 CenterZ=0 NormalX=0 NormalY=0 NormalZ=1 Radius=1
    g1: LineSegment [constr] StartX=-20.15 StartY=10 StartZ=0 EndX=-18.35 EndY=8.2 EndZ=0
    g2: LineSegment [constr] StartX=-20.15 StartY=10 StartZ=0 EndX=0 EndY=10 EndZ=0
    g3: Circle CenterX=-17.6429 CenterY=-7.49289 CenterZ=0 NormalX=0 NormalY=0 NormalZ=1 Radius=1
    g4: Circle CenterX=17.6429 CenterY=7.49289 CenterZ=0 NormalX=0 NormalY=0 NormalZ=1 Radius=1
    g5: Circle CenterX=17.6429 CenterY=-7.49289 CenterZ=0 NormalX=0 NormalY=0 NormalZ=1 Radius=1
  constraints (15):
    c: Radius(g0) = 1
    c: Coincident(g2,g1)
    c: Horizontal(g2)
    c: PointOnObject(g2,g-2)
    c: Angle(g1,g2) = 0.785398
    c: PointOnObject(g1,g0)
    c: PointOnObject(g0,g1)
    c: Coincident(g1,g-3)
    c: DistanceX(g1,g1) = -1.8
    c: Equal(g0,g3)
    c: Equal(g3,g5)
    c: Equal(g5,g4)
    c: Symmetric(g0,g3,g-1)
    c: Symmetric(g0,g4,g-2)
    c: Symmetric(g0,g5,g-1)
FEATURE [PartDesign::Pocket] Pocket002008007004  label="servo-body-final-1"
  Length = 30
  Sketch = -> Sketch026
  Type = 0
FEATURE [Part::Fillet] Fillet001007  label="servo-body-final-rounded"
  Base = -> Pocket002008007004
  Edges = 24 edges r=0.6: [Edge2,Edge5,Edge18,Edge24,Edge25,Edge26,Edge29,Edge30,Edge32,Edge33,Edge36,Edge39,Edge40,Edge41,Edge43,Edge46,Edge52,Edge53,Edge56,Edge59,Edge62,Edge77,Edge93,Edge95]
FEATURE [App::DocumentObjectGroup] Group005  label="servo-body"
  Group = -> [Pad,Pocket,Fusion006,Pocket002008004,Pocket002008007002,Pocket002008007003,Mirrored,Pocket002008007004,Fillet001007]
FEATURE [Part::MultiFuse] Fusion001  label="ears-final"
  Placement = pos=(0,0,25.8) rot=(0,0,1;0rad)
  Shapes = -> [Pocket004,Pad002]
FEATURE [Part::Fillet] Fillet001008  label="ears-final-rounded"
  Base = -> Fusion001
  Edges = 4 edges r=0.6: [Edge1,Edge2,Edge5,Edge8]
FEATURE [App::DocumentObjectGroup] Group001  label="servo-ears"
  Group = -> [Pad001,Pocket004,Pad002,Fusion001,Fillet001008]
FEATURE [Part::Feature] Fillet001007001  label="servo-body-1"
  shape: bbox 40.3 x 20 x 36.49 mm, 79 faces (baked)
FEATURE [Part::Mirroring] Part__Mirroring001  label="cone-2"
  Base = (0,0,0)
  Normal = (0,1,0)
  Source = -> Loft002
FEATURE [Part::MultiFuse] Fusion  label="two-top-cones"
  Shapes = -> [Loft002,Part__Mirroring001]
FEATURE [App::DocumentObjectGroup] Group006  label="top-cone"
  Group = -> [Loft002,Part__Mirroring001,Fusion]
FEATURE [Part::Feature] Fusion007  label="two-top-cones-1"
  shape: bbox 2.5 x 13.7 x 0.6 mm, 6 faces, 2 solids (baked)
FEATURE [Part::Cut] Cut  label="servo-body-2"
  Base = -> Fillet001007001
  Tool = -> Fusion007
FEATURE [Part::Feature] Pocket002008007005  label="servo-shaft-1"
  Placement = pos=(9.45,0,36) rot=(0,0,1;0rad)
  shape: bbox 14.4 x 14.4 x 5.74 mm, 155 faces (baked)
FEATURE [Part::Feature] Fillet001008001  label="servo-ears-1"
  shape: bbox 55.5 x 18.1 x 4.1 mm, 21 faces (baked)
FEATURE [Part::Feature] Pocket002008007006  label="Servo-wire-holder-1"
  Placement = pos=(20.15,0,2.9) rot=(0,0,1;0rad)
  shape: bbox 1.8 x 6.7 x 4.2 mm, 11 faces (baked)
FEATURE [Part::MultiFuse] Fusion008  label="Servo-no-screws"
  Shapes = -> [Cut,Fillet001008001,Pocket002008007006,Pocket002008007005]
FEATURE [Part::MultiFuse] Fusion009  label="servo-screws"
  Shapes = -> [Fillet001,Fillet001001,Fillet001002,Fillet001003]
FEATURE [App::DocumentObjectGroup] Group004  label="Servo-bottom-screws"
  Group = -> [Revolution,Pocket002006,Fillet,Fillet001,Fillet001001,Fillet001002,Fillet001003,Fusion009]
FEATURE [Part::Feature] Fusion009001  label="servo-screws-four"
  shape: bbox 38.86 x 18.56 x 28.9 mm, 76 faces, 4 solids (baked)
FEATURE [Part::MultiFuse] Fusion009002  label="Servo-Futaba3003-final"
  Shapes = -> [Fusion008,Fusion009001]
FEATURE [Part::MultiFuse] Fusion009003  label="servo-wires"
  Placement = pos=(20,0,2.9) rot=(0,0,1;0rad)
  Shapes = -> [Cylinder,Cylinder002,Cylinder001]
FEATURE [Part::Feature] Fusion009002001  label="Servo-Futaba3003-final001"
  shape: bbox 55.5 x 20 x 41.74 mm, 365 faces (baked)
FEATURE [Part::Feature] Fusion009003001  label="servo-wires001"
  Placement = pos=(20,0,2.9) rot=(0,0,1;0rad)
  shape: bbox 10 x 3.6 x 1.2 mm, 13 faces, 3 solids (baked)
FEATURE [Part::Compound] Compound  label="Servo-Futaba-3003-ready"
  Links = -> [Fusion009002001,Fusion009003001]
